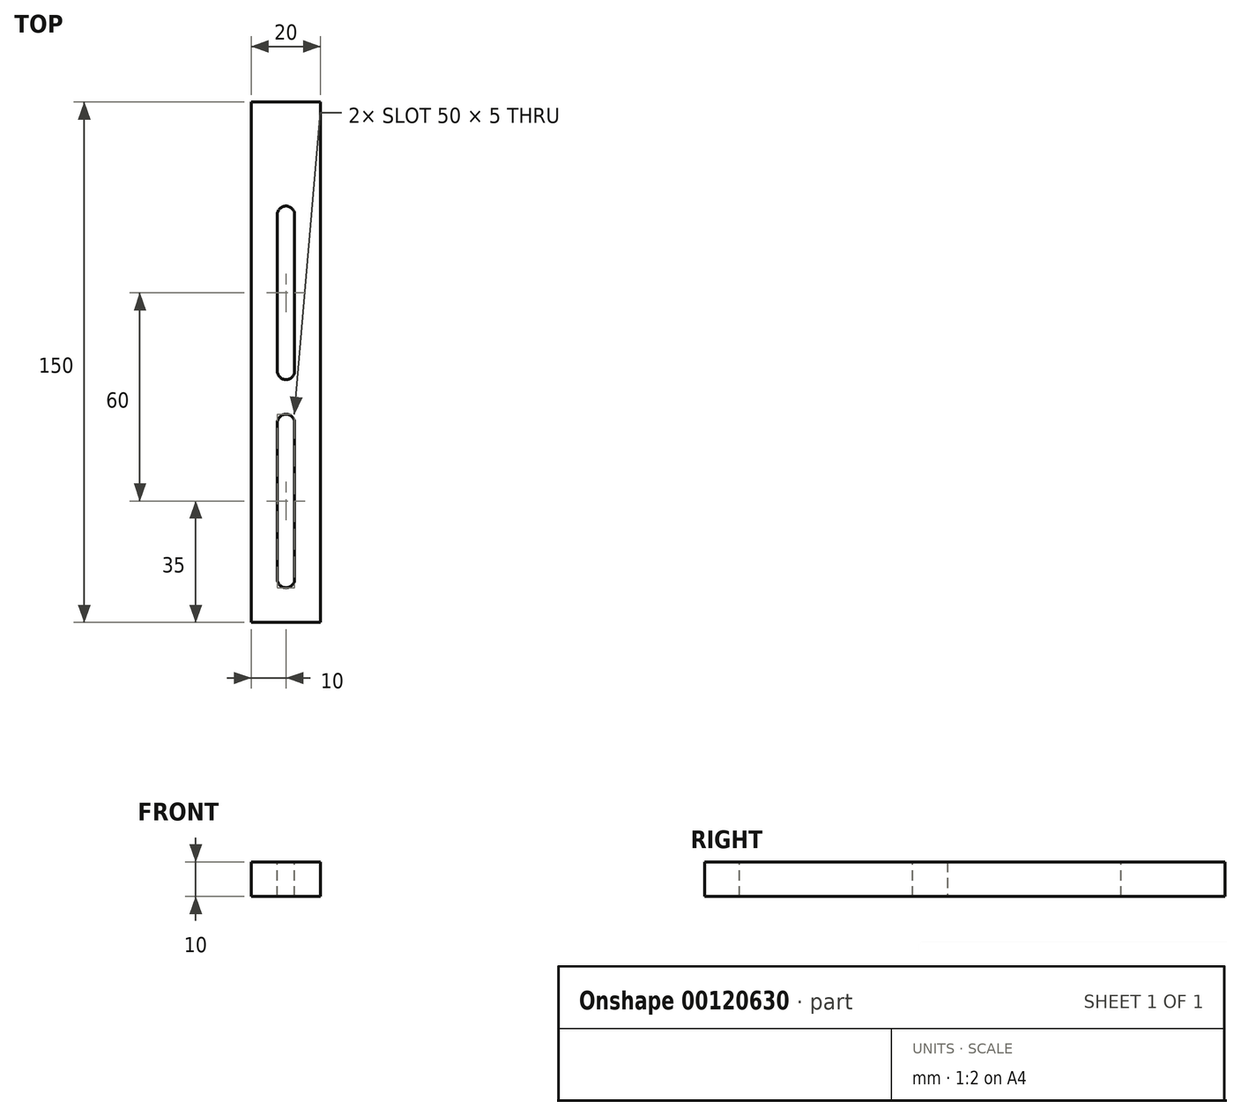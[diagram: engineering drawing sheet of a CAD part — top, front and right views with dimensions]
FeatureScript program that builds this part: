
annotation { "Feature Type Name" : "Feature", "Feature Type Description" : "" }
export const myFeature = defineFeature(function(context is Context, id is Id, definition is map)
    precondition{}
    {
        {
            var Q0;
            Q0=qCreatedBy(makeId("Top.planeOp"),FACE);
            var sketch = newSketch(context, id + "F0", { "sketchPlane" : qUnion([Q0])});
            skLineSegment(sketch, "E0.bottom", {"start": v(0, 0) * mm, "end": v(20, 0) * mm});
            skLineSegment(sketch, "E0.top", {"start": v(0, 150) * mm, "end": v(20, 150) * mm});
            skLineSegment(sketch, "E0.left", {"start": v(0, 0) * mm, "end": v(0, 150) * mm});
            skLineSegment(sketch, "E0.right", {"start": v(20, 0) * mm, "end": v(20, 150) * mm});
            skSolve(sketch);
        }
        {
            var Q0;
            Q0=makeQuery(id+"F0.imprint","IMPRINT",FACE,{"disambiguationData":[TD([[makeQuery(id+"F0.imprint","IMPRINT",EDGE,{"derivedFrom":sQuery(id+"F0.wireOp",EDGE,"E0.bottom")}),1.0]])]});
            extrude(context, id + "F1", {"entities" : qUnion([Q0]), "depth" : 10 * mm});
        }
        {
            var Q0;
            Q0=makeQuery(id+"F1.opExtrude","CAP_FACE",FACE,{"disambiguationData":[OSD([sQuery(id+"F0.wireOp",EDGE,"E0.bottom"),sQuery(id+"F0.wireOp",EDGE,"E0.top"),sQuery(id+"F0.wireOp",EDGE,"E0.left"),sQuery(id+"F0.wireOp",EDGE,"E0.right")])],"isStart":false});
            var sketch = newSketch(context, id + "F2", { "sketchPlane" : qUnion([Q0])});
            skLineSegment(sketch, "E1.bottom", {"start": v(7.5, 10) * mm, "end": v(12.5, 10) * mm});
            skLineSegment(sketch, "E1.top", {"start": v(7.5, 60) * mm, "end": v(12.5, 60) * mm});
            skLineSegment(sketch, "E1.left", {"start": v(7.5, 10) * mm, "end": v(7.5, 60) * mm});
            skLineSegment(sketch, "E1.right", {"start": v(12.5, 10) * mm, "end": v(12.5, 60) * mm});
            skLineSegment(sketch, "E2", {"start": v(0, 65) * mm, "end": v(20, 65) * mm, "construction": true});
            skLineSegment(sketch, "E3.MirrorCS", {"start": v(7.5, 120) * mm, "end": v(7.5, 70) * mm});
            skLineSegment(sketch, "E4.MirrorCS", {"start": v(7.5, 120) * mm, "end": v(12.5, 120) * mm});
            skLineSegment(sketch, "E5.MirrorCS", {"start": v(12.5, 120) * mm, "end": v(12.5, 70) * mm});
            skLineSegment(sketch, "E6.MirrorCS", {"start": v(7.5, 70) * mm, "end": v(12.5, 70) * mm});
            skSolve(sketch);
        }
        {
            var Q0;
            Q0=makeQuery(id+"F2.imprint","IMPRINT",FACE,{"disambiguationData":[TD([[makeQuery(id+"F2.imprint","IMPRINT",EDGE,{"derivedFrom":sQuery(id+"F2.wireOp",EDGE,"E3.MirrorCS")}),1.0]])]});
            var Q1;
            Q1=makeQuery(id+"F2.imprint","IMPRINT",FACE,{"disambiguationData":[TD([[makeQuery(id+"F2.imprint","IMPRINT",EDGE,{"derivedFrom":sQuery(id+"F2.wireOp",EDGE,"E1.bottom")}),1.0]])]});
            extrude(context, id + "F3", {"entities" : qUnion([Q0, Q1]), "operationType" : NewBodyOperationType.REMOVE, "oppositeDirection" : true, "depth" : 25 * mm});
        }
        {
            var Q0;
            Q0=makeQuery(id+"F3.boolean.opBoolean","COPY",EDGE,{"derivedFrom":makeQuery(id+"F3.opExtrude","SWEPT_EDGE",EDGE,{"disambiguationData":[OSD([sQuery(id+"F2.wireOp",EDGE,"E1.top"),sQuery(id+"F2.wireOp",EDGE,"E1.right")])]})});
            var Q1;
            Q1=makeQuery(id+"F3.boolean.opBoolean","COPY",EDGE,{"derivedFrom":makeQuery(id+"F3.opExtrude","SWEPT_EDGE",EDGE,{"disambiguationData":[OSD([sQuery(id+"F2.wireOp",EDGE,"E1.top"),sQuery(id+"F2.wireOp",EDGE,"E1.left")])]})});
            var Q2;
            Q2=makeQuery(id+"F3.boolean.opBoolean","COPY",EDGE,{"derivedFrom":makeQuery(id+"F3.opExtrude","SWEPT_EDGE",EDGE,{"disambiguationData":[OSD([sQuery(id+"F2.wireOp",EDGE,"E3.MirrorCS"),sQuery(id+"F2.wireOp",EDGE,"E4.MirrorCS")])]})});
            var Q3;
            Q3=makeQuery(id+"F3.boolean.opBoolean","COPY",EDGE,{"derivedFrom":makeQuery(id+"F3.opExtrude","SWEPT_EDGE",EDGE,{"disambiguationData":[OSD([sQuery(id+"F2.wireOp",EDGE,"E4.MirrorCS"),sQuery(id+"F2.wireOp",EDGE,"E5.MirrorCS")])]})});
            var Q4;
            Q4=makeQuery(id+"F3.boolean.opBoolean","COPY",EDGE,{"derivedFrom":makeQuery(id+"F3.opExtrude","SWEPT_EDGE",EDGE,{"disambiguationData":[OSD([sQuery(id+"F2.wireOp",EDGE,"E3.MirrorCS"),sQuery(id+"F2.wireOp",EDGE,"E6.MirrorCS")])]})});
            var Q5;
            Q5=makeQuery(id+"F3.boolean.opBoolean","COPY",EDGE,{"derivedFrom":makeQuery(id+"F3.opExtrude","SWEPT_EDGE",EDGE,{"disambiguationData":[OSD([sQuery(id+"F2.wireOp",EDGE,"E1.bottom"),sQuery(id+"F2.wireOp",EDGE,"E1.left")])]})});
            var Q6;
            Q6=makeQuery(id+"F3.boolean.opBoolean","COPY",EDGE,{"derivedFrom":makeQuery(id+"F3.opExtrude","SWEPT_EDGE",EDGE,{"disambiguationData":[OSD([sQuery(id+"F2.wireOp",EDGE,"E1.bottom"),sQuery(id+"F2.wireOp",EDGE,"E1.right")])]})});
            var Q7;
            Q7=makeQuery(id+"F3.boolean.opBoolean","COPY",EDGE,{"derivedFrom":makeQuery(id+"F3.opExtrude","SWEPT_EDGE",EDGE,{"disambiguationData":[OSD([sQuery(id+"F2.wireOp",EDGE,"E5.MirrorCS"),sQuery(id+"F2.wireOp",EDGE,"E6.MirrorCS")])]})});
            fillet(context, id + "F4", {"entities" : qUnion([Q0, Q1, Q2, Q3, Q4, Q5, Q6, Q7]), "radius" : 2.5 * mm, "tangentPropagation" : true, "allowEdgeOverflow" : false});
        }
    });
